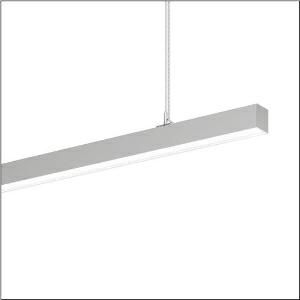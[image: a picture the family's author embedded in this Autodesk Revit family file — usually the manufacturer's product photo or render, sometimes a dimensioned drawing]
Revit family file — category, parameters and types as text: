
# Revit family: silica_r__21_51mx33tbt9s_9dae
name_source: partatom
category: Lighting Fixtures
units: mm (PartAtom-declared; Revit-internal decimal feet)

## family parameters
Cut with Voids When Loaded = No
Host = Face
Light Source = No
Part Type = Normal
Room Calculation Point = No
Round Connector Dimension = Use Diameter
Shared = No

## types (1)
- --- (1 x LED, 7170 lm, 67.4 W, 6500K)
    Apparent Load = 67 VA
    CIE Flux Codes = 78 96 99 56 100
    Color Rendering = 80
    Color Temperature = 6500K
    Default Elevation = 1800 mm
    Description = Silica® 21, office luminaire, primary optical cover: prismatic diffuser, of PMMA, CAT 2 (L<= 3000cd/m²), light emission: direct/indirect distribution, primary light characteristic: symmetric, installation type: suspended mounting, LED, rated luminous flux: 7.170lm, luminous efficacy: 101lm/W, light colour: 8tw, colour temperature: 2700..6500K, control gear: ECG DALI, with terminal, 3+2-pole, max. 2.5mm², mains connection: 220..240V, AC, 50/60Hz, rated input power: 70.8W, luminaire housing, of aluminium, metallic grey (RAL 9006), length: 1.504mm, width: 53mm, height: 53mm, protection rating (complete): IP20, insulation class (complete): insulation class I (protective earthing), certification: CE, permissible operating ambient temperature: 0..+35°C, standard: EN 50419, packaging unit: 1 piece
    Height = 53 mm
    Lamp = 1 x LED
    Lamp Light Flux = 7170 lm
    Lamp Power = 67.4 W
    Lamp count = 1
    Length = 1504 mm
    Luminous efficacy = 106 lm/W
    Manufacturer = Siteco
    ModVariant = No
    Model = 51MX33TBT9S
    Mounting Place = Ceiling
    Mounting Type = Pendant
    Number of Poles = 1
    OnlyDefault = Yes
    Power Factor = 1
    Product Name = Silica® 21
    Product group = office luminaire | ceiling pendant
    ProductGroupID = 902
    Protection Class = Protection class I
    Protection Degree = IP 20
    RLX_Detail_Level = 1
    RLX_Emergency_Light_Flux = 0 lm
    RLX_Emergency_Type = 0
    RLX_Emergency_Type_DB = No
    RlxData = <blob elided: 20189 chars, md5=e1e912a8>
    Socket = socket
    Standby Power = 0 W
    System Light Flux = 7170 lm
    System Power = 67 W
    Type Comments = individual setting
    Type Image = l_1313621.jpg
    URL = http://relux.com
    VarID = @adj_089109
    Voltage = 0 V
    Weight = 0.00 kg
    Width = 53 mm

## geometry (parser evidence)
native form markers: Blend x4, Sweep x14
no freeform markers — native parametric forms only
